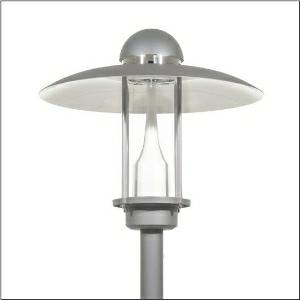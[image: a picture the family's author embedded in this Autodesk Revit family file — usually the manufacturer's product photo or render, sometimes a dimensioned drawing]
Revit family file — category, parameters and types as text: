
# Revit family: city-light_elegance_iq___p1_0a_5xa5265ff14h000022_f356
name_source: partatom
category: Lighting Fixtures
units: mm (PartAtom-declared; Revit-internal decimal feet)

## family parameters
Cut with Voids When Loaded = No
Host = Face
Light Source = No
Part Type = Normal
Room Calculation Point = No
Round Connector Dimension = Use Diameter
Shared = No

## types (1)
- --- (1 x LED, 1440 lm, 10.5 W, 3000K)
    Apparent Load = 11 VA
    CIE Flux Codes = 32 62 91 97 100
    Color Rendering = 70
    Color Temperature = 3000K
    Default Elevation = 1800 mm
    Description = City-Light Elegance iQ, mast luminaire, Module 540 iQ-SR, primary light control with 3 zone facetted reflector, of plastic, silver coated, highly specular, structured, primary optical cover: cover, of PMMA, transparent, light distribution: P1.0a, light emission: direct distribution, primary light characteristic: strongly asymmetric, installation type: post-top, LED, High Power LED, rated luminous flux: 1.440lm, luminous efficacy: 137lm/W, light colour: 730, colour temperature: 3000K, control gear: iQ Street-Remote, control: Street-Remote, Auto-Match, Temp-Guard, Lumen-Switch, Night-Set, Smart-Wire, Light-Fading, Desk-Remote (wireless, voltage-free reading and setting of iQ features in the workshop via application-optimized NFC function/RFID function), optimised constant luminous flux control (CLO 2.0), pre-setting: logarithmic dimming characteristic, mains connection: 230..240V, AC, 50/60Hz, connection cable pre-assembled, cable length: 5,5m, wiring characteristics: H07RN-F, start of lifetime: 11W, end of service life: 11W, reduction: 5W, luminaire housing, upper part, of aluminium, coated, Siteco® metallic grey (DB 702S), diameter: 750mm, height: 675mm, spigot size: d x l = 76 x 70mm (post-top) | with reducer (optional accessory) 60 x 70mm, mounting height: 3..5m, post-top mast mounting element, of diecast aluminium, coated, Siteco® metallic grey (DB 702S), Module 540 iQ-SR, traffic white (RAL 9016), equipment: standard, protection rating (complete): IP65, insulation class (complete): insulation class II (safety insulation), certification: CE, ENEC, VDE, packaging unit: 1 piece

Light Distribution: P1.0a
    Height = 675 mm
    Lamp = 1 x LED
    Lamp Light Flux = 1440 lm
    Lamp Power = 10.5 W
    Lamp count = 1
    Length = 750 mm
    Luminous efficacy = 137 lm/W
    Manufacturer = Siteco
    ModVariant = No
    Model = 5XA5265FF14H000022
    Number of Poles = 1
    OnlyDefault = Yes
    Power Factor = 1
    Product Name = City-Light Elegance iQ | P1.0a
    Product group = mast luminaire | pylon top
    ProductGroupID = 6100
    Protection Class = Protection class II
    Protection Degree = IP 65
    RLX_Detail_Level = 1
    RLX_Emergency_Light_Flux = 0 lm
    RLX_Emergency_Type = 0
    RLX_Emergency_Type_DB = No
    RlxData = <blob elided: 35809 chars, md5=b65de8c6>
    Socket = socket
    Standby Power = 0 W
    System Light Flux = 1440 lm
    System Power = 11 W
    Type Comments = factory setting: luminous flux: 100 % | dim-lin: 254 | 419 mA
    Type Image = l_1006912.jpg
    URL = http://relux.com
    VarID = @adj_159686
    Voltage = 0 V
    Weight = 0.00 kg
    Width = 0 mm  [stored 0 ft]

note: [stored X ft] marks values corroborated as IEEE doubles in the binary element streams (Revit-internal decimal feet)

## geometry (parser evidence)
native form markers: Blend x4, Sweep x11
no freeform markers — native parametric forms only
